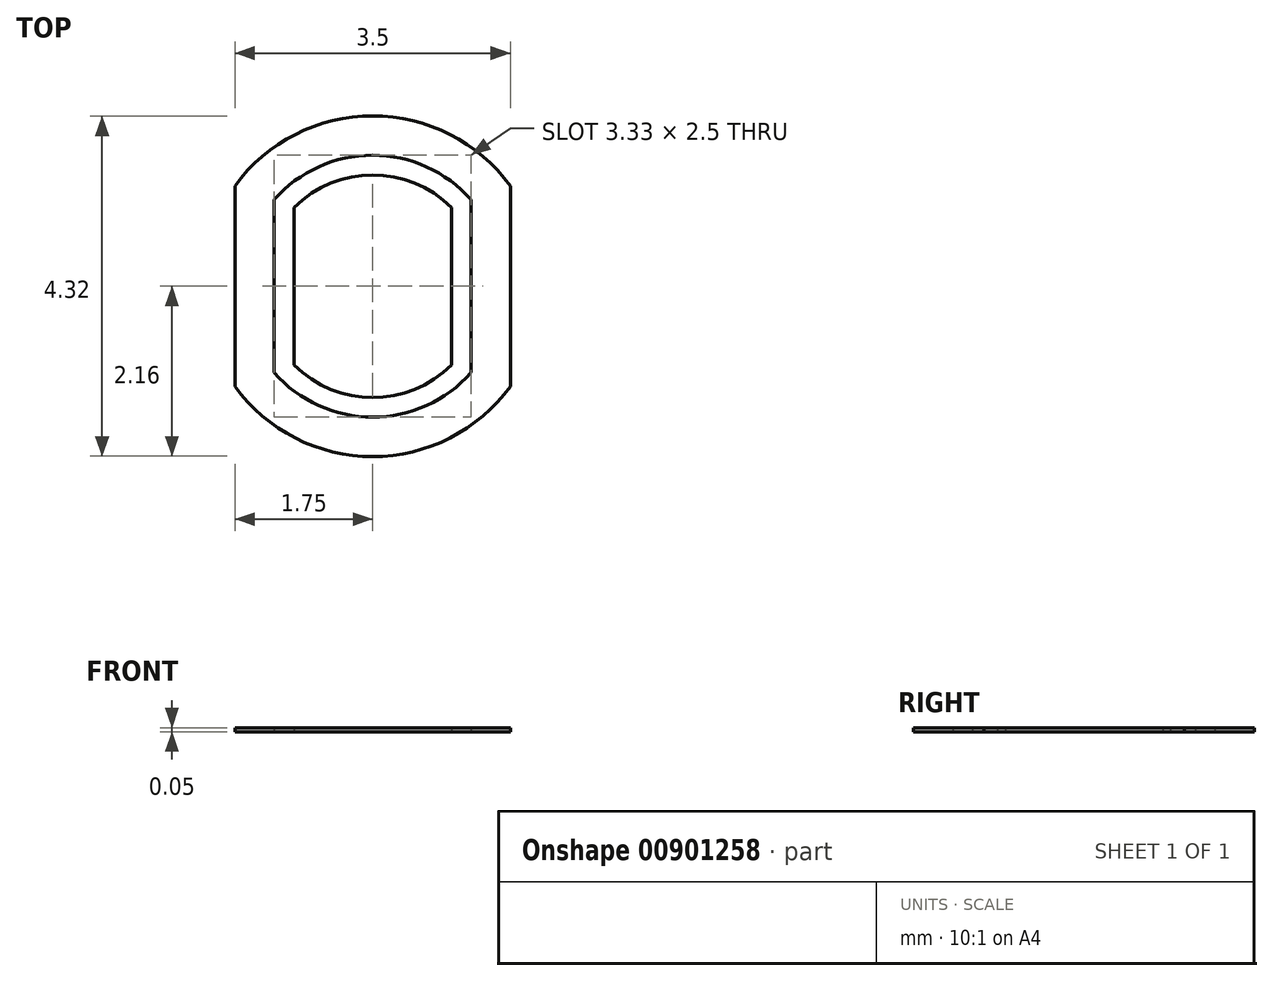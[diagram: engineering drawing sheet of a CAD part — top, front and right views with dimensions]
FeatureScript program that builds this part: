
annotation { "Feature Type Name" : "Feature", "Feature Type Description" : "" }
export const myFeature = defineFeature(function(context is Context, id is Id, definition is map)
    precondition{}
    {
        {
            var Q0;
            Q0=qCreatedBy(makeId("Top.planeOp"),FACE);
            var sketch = newSketch(context, id + "F0", { "sketchPlane" : qUnion([Q0])});
            skLineSegment(sketch, "E0.bottom", {"start": v(-1, 1) * mm, "end": v(1, 1) * mm, "construction": true});
            skLineSegment(sketch, "E0.top", {"start": v(-1, -1) * mm, "end": v(1, -1) * mm, "construction": true});
            skLineSegment(sketch, "E0.left", {"start": v(-1, 1) * mm, "end": v(-1, -1) * mm});
            skLineSegment(sketch, "E0.right", {"start": v(1, 1) * mm, "end": v(1, -1) * mm});
            skPoint(sketch, "E1", {"position": v(-1, 0) * mm});
            skPoint(sketch, "E2", {"position": v(0, 1) * mm});
            skArc(sketch, "E3", {"start": v(1, 1) * mm, "mid": v(0, 1.41) * mm, "end": v(-1, 1) * mm});
            skArc(sketch, "E4", {"start": v(-1, -1) * mm, "mid": v(0, -1.41) * mm, "end": v(1, -1) * mm});
            skLineSegment(sketch, "E5.0", {"start": v(-1.25, 1.1) * mm, "end": v(-1.25, -1.1) * mm});
            skArc(sketch, "E5.1", {"start": v(1.25, 1.1) * mm, "mid": v(0, 1.66) * mm, "end": v(-1.25, 1.1) * mm});
            skLineSegment(sketch, "E5.2", {"start": v(1.25, 1.1) * mm, "end": v(1.25, -1.1) * mm});
            skArc(sketch, "E5.3", {"start": v(-1.25, -1.1) * mm, "mid": v(0, -1.66) * mm, "end": v(1.25, -1.1) * mm});
            skArc(sketch, "E6.0", {"start": v(1.75, 1.27) * mm, "mid": v(0, 2.16) * mm, "end": v(-1.75, 1.27) * mm});
            skLineSegment(sketch, "E6.1", {"start": v(1.75, 1.27) * mm, "end": v(1.75, -1.27) * mm});
            skArc(sketch, "E6.2", {"start": v(-1.75, -1.27) * mm, "mid": v(0, -2.16) * mm, "end": v(1.75, -1.27) * mm});
            skLineSegment(sketch, "E6.3", {"start": v(-1.75, 1.27) * mm, "end": v(-1.75, -1.27) * mm});
            skSolve(sketch);
        }
        {
            var Q0;
            Q0=makeQuery(id+"F0.imprint","IMPRINT",FACE,{"disambiguationData":[TD([[makeQuery(id+"F0.imprint","IMPRINT",EDGE,{"derivedFrom":sQuery(id+"F0.wireOp",EDGE,"E5.0")}),-1.0]])]});
            var Q1;
            Q1=makeQuery(id+"F0.imprint","IMPRINT",FACE,{"disambiguationData":[TD([[makeQuery(id+"F0.imprint","IMPRINT",EDGE,{"derivedFrom":sQuery(id+"F0.wireOp",EDGE,"E0.left")}),1.0]])]});
            extrude(context, id + "F1", {"entities" : qUnion([Q0, Q1]), "depth" : 0.05 * mm, "offsetDistance" : 25 * mm});
        }
    });
